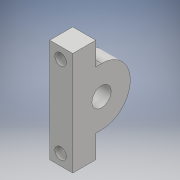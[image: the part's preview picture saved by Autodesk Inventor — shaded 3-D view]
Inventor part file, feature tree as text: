
AUTODESK INVENTOR PART (.ipt)
format: ipt  version: 2017 (Build 210142000, 142)  size: 135,168 bytes
history: native  units: mm
features: extrude x3, sketch x3
ambient origin geometry x8: Origin, YZ Plane, XZ Plane, XY Plane, X Axis, Y Axis, Z Axis, Center Point
bodies: Solid1 (feature_tree)
feature tree (6):
  extrude  "Extrusion1"  Depth=7.5mm
  extrude  "Extrusion2"  Depth=3.0mm
  extrude  "Extrusion3"  Depth=10.0mm
  sketch  "Sketch1"  dims[d0=2.5mm d1=7.5mm]
  sketch  "Sketch2"  dims[d2=3.0mm d3=3.0mm]
  sketch  "Sketch3"  dims[d4=3.0mm d5=0.0mm d6=2.5mm d7=10.0mm d8=0.0mm d9=1.5mm d10=10.0mm d11=0.0mm]
